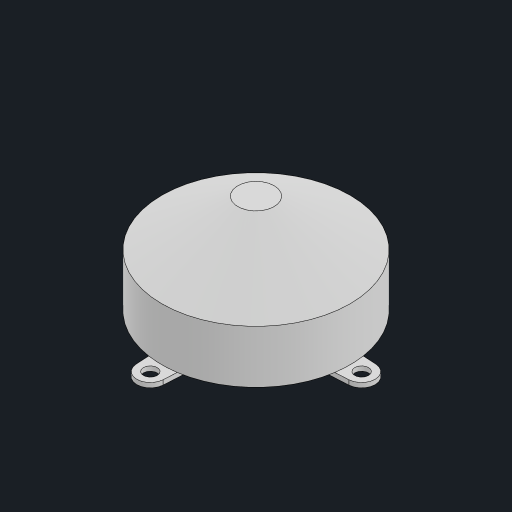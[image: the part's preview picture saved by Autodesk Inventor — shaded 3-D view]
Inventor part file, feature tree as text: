
AUTODESK INVENTOR PART (.ipt)
format: ipt  version: 2023 (Build 270158000, 158)  size: 166,912 bytes
history: native  units: mm
features: sketch x2, other x1, revolve x1, extrude x1, projected_geometry x1
ambient origin geometry x8: Origin, YZ Plane, XZ Plane, XY Plane, X Axis, Y Axis, Z Axis, Center Point
bodies: Body1 (feature_tree)
feature tree (6):
  other  "ソリッド1"
  revolve  "回転1"
  extrude  "押し出し1"  Depth=14.25mm
  sketch  "スケッチ1"
  sketch  "スケッチ2"
  projected_geometry  "投影ループ1"
